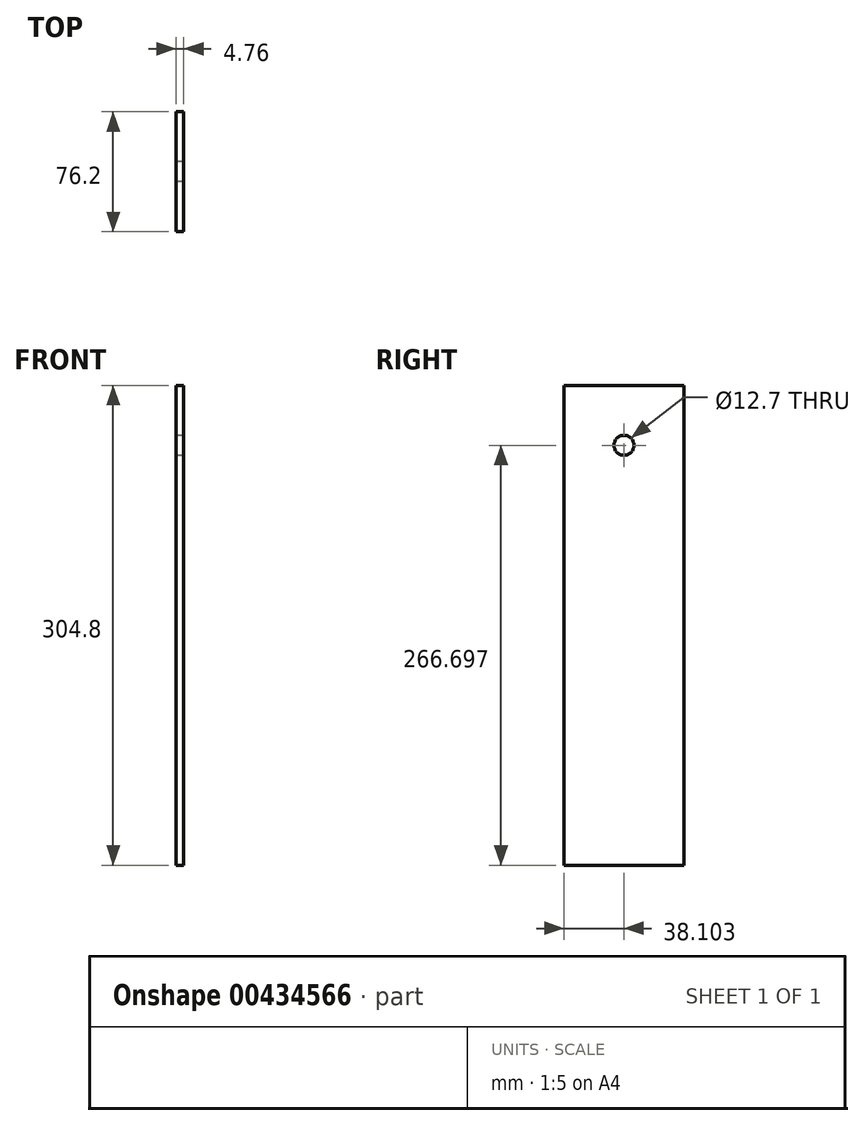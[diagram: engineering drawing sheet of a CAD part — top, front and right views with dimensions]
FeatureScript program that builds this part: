
annotation { "Feature Type Name" : "Feature", "Feature Type Description" : "" }
export const myFeature = defineFeature(function(context is Context, id is Id, definition is map)
    precondition{}
    {
        {
            var Q0;
            Q0=qCreatedBy(makeId("Right.planeOp"),FACE);
            var sketch = newSketch(context, id + "F0", { "sketchPlane" : qUnion([Q0])});
            skLineSegment(sketch, "E0.bottom", {"start": v(-54.8, 279.96) * mm, "end": v(21.4, 279.96) * mm});
            skLineSegment(sketch, "E0.top", {"start": v(-54.8, -24.84) * mm, "end": v(21.4, -24.84) * mm});
            skLineSegment(sketch, "E0.left", {"start": v(-54.8, 279.96) * mm, "end": v(-54.8, -24.84) * mm});
            skLineSegment(sketch, "E0.right", {"start": v(21.4, 279.96) * mm, "end": v(21.4, -24.84) * mm});
            skCircle(sketch, "E1", {"center": v(-16.7, 241.86) * mm, "radius": 6.35 * mm});
            skSolve(sketch);
        }
        {
            var Q0;
            Q0=makeQuery(id+"F0.imprint","IMPRINT",FACE,{"disambiguationData":[TD([[makeQuery(id+"F0.imprint","IMPRINT",EDGE,{"derivedFrom":sQuery(id+"F0.wireOp",EDGE,"E0.bottom")}),-1.0]])]});
            extrude(context, id + "F1", {"entities" : qUnion([Q0]), "depth" : 4.76 * mm});
        }
    });
